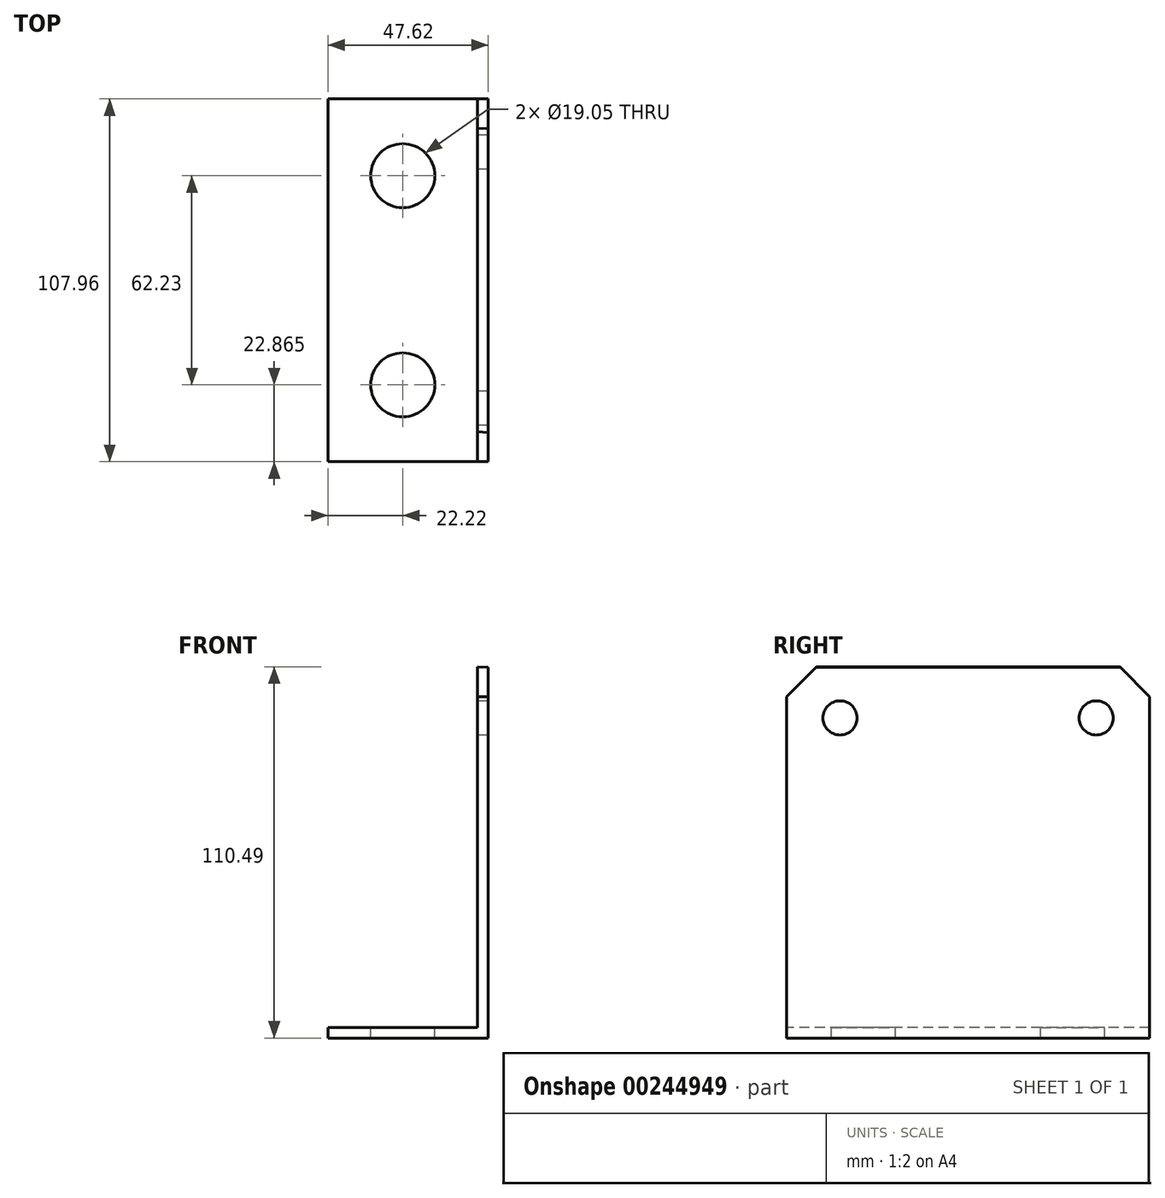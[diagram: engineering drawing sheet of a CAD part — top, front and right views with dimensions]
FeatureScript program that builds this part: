
annotation { "Feature Type Name" : "Feature", "Feature Type Description" : "" }
export const myFeature = defineFeature(function(context is Context, id is Id, definition is map)
    precondition{}
    {
        {
            var Q0;
            Q0=qCreatedBy(makeId("Right.planeOp"),FACE);
            var sketch = newSketch(context, id + "F0", { "sketchPlane" : qUnion([Q0])});
            skLineSegment(sketch, "E0.bottom", {"start": v(28.57, 63.5) * mm, "end": v(-28.57, 63.5) * mm});
            skLineSegment(sketch, "E0.top", {"start": v(53.97, -63.5) * mm, "end": v(-53.97, -63.5) * mm});
            skLineSegment(sketch, "E0.left", {"start": v(53.98, 38.1) * mm, "end": v(53.98, -63.5) * mm});
            skLineSegment(sketch, "E0.right", {"start": v(-53.98, 38.1) * mm, "end": v(-53.97, -63.5) * mm});
            skPoint(sketch, "E0.middle", {"position": v(0, 0) * mm});
            skLineSegment(sketch, "E1", {"start": v(0, 0) * mm, "end": v(0, 94.6) * mm, "construction": true});
            skPoint(sketch, "E1.endSnap0", {"position": v(0, 63.5) * mm});
            skLineSegment(sketch, "E2", {"start": v(-53.98, 38.1) * mm, "end": v(-28.57, 63.5) * mm});
            skLineSegment(sketch, "E3.MirrorCS", {"start": v(53.97, 38.1) * mm, "end": v(28.57, 63.5) * mm});
            skPoint(sketch, "E4.orphan", {"position": v(-53.98, 63.5) * mm});
            skPoint(sketch, "E5.orphan", {"position": v(53.98, 63.5) * mm});
            skSolve(sketch);
        }
        {
            var Q0;
            Q0=qSketchRegion(id+"F0",true);
            extrude(context, id + "F1", {"entities" : qUnion([Q0]), "depth" : 3.17 * mm});
        }
        {
            var Q0;
            Q0=makeQuery(id+"F1.opExtrude","SWEPT_FACE",FACE,{"disambiguationData":[OSD([sQuery(id+"F0.wireOp",EDGE,"E0.right")])]});
            var sketch = newSketch(context, id + "F2", { "sketchPlane" : qUnion([Q0])});
            skLineSegment(sketch, "E6", {"start": v(3.18, -63.5) * mm, "end": v(47.62, -63.5) * mm});
            skLineSegment(sketch, "E7", {"start": v(47.62, -63.5) * mm, "end": v(47.62, -60.33) * mm});
            skLineSegment(sketch, "E8", {"start": v(47.62, -60.33) * mm, "end": v(3.17, -60.33) * mm});
            skLineSegment(sketch, "E9", {"start": v(3.17, -60.33) * mm, "end": v(3.18, -63.5) * mm});
            skSolve(sketch);
        }
        {
            var Q0;
            Q0=qSketchRegion(id+"F2",true);
            var Q1;
            Q1=makeQuery(id+"F1.opExtrude","SWEPT_FACE",FACE,{"disambiguationData":[OSD([sQuery(id+"F0.wireOp",EDGE,"E0.left")])]});
            extrude(context, id + "F3", {"entities" : qUnion([Q0]), "operationType" : NewBodyOperationType.ADD, "endBound" : BoundingType.UP_TO_SURFACE, "oppositeDirection" : true, "endBoundEntityFace" : qUnion([Q1]), "depth" : 25.4 * mm});
        }
        {
            var Q0;
            Q0=makeQuery(id+"F1.opExtrude","CAP_FACE",FACE,{"disambiguationData":[OSD([sQuery(id+"F0.wireOp",EDGE,"E0.bottom"),sQuery(id+"F0.wireOp",EDGE,"E0.top"),sQuery(id+"F0.wireOp",EDGE,"E0.left"),sQuery(id+"F0.wireOp",EDGE,"E0.right")])],"isStart":false});
            var sketch = newSketch(context, id + "F4", { "sketchPlane" : qUnion([Q0])});
            skCircle(sketch, "E10", {"center": v(-38.1, 31.75) * mm, "radius": 5.08 * mm});
            skCircle(sketch, "E11", {"center": v(38.1, 31.75) * mm, "radius": 5.08 * mm});
            skSolve(sketch);
        }
        {
            var Q0;
            Q0=qSketchRegion(id+"F4",true);
            var Q1;
            Q1=makeQuery(id+"F1.opExtrude","CAP_FACE",FACE,{"disambiguationData":[OSD([sQuery(id+"F0.wireOp",EDGE,"E0.bottom"),sQuery(id+"F0.wireOp",EDGE,"E0.top"),sQuery(id+"F0.wireOp",EDGE,"E0.left"),sQuery(id+"F0.wireOp",EDGE,"E0.right"),sQuery(id+"F0.wireOp",EDGE,"E2"),sQuery(id+"F0.wireOp",EDGE,"E3.MirrorCS")])],"isStart":true});
            extrude(context, id + "F5", {"entities" : qUnion([Q0]), "operationType" : NewBodyOperationType.REMOVE, "endBound" : BoundingType.UP_TO_SURFACE, "oppositeDirection" : true, "endBoundEntityFace" : qUnion([Q1]), "depth" : 25.4 * mm});
        }
        {
            var Q0;
            Q0=makeQuery(id+"F3.opExtrude","SWEPT_FACE",FACE,{"disambiguationData":[OSD([sQuery(id+"F2.wireOp",EDGE,"E8")])]});
            var sketch = newSketch(context, id + "F6", { "sketchPlane" : qUnion([Q0])});
            skLineSegment(sketch, "E12", {"start": v(0, 0) * mm, "end": v(0, 50.21) * mm, "construction": true});
            skPoint(sketch, "E13.centerSnap0", {"position": v(25.4, -53.97) * mm});
            skLineSegment(sketch, "E14", {"start": v(0, 0) * mm, "end": v(-46.47, 0) * mm, "construction": true});
            skCircle(sketch, "E15", {"center": v(25.4, 31.11) * mm, "radius": 9.53 * mm});
            skPoint(sketch, "E15.centerSnap0", {"position": v(25.4, 53.97) * mm});
            skCircle(sketch, "E16.MirrorC", {"center": v(25.4, -31.11) * mm, "radius": 9.53 * mm});
            skSolve(sketch);
        }
        {
            var Q0;
            Q0=qSketchRegion(id+"F6",true);
            var Q1;
            Q1=makeQuery(id+"F3.boolean.opBoolean","MERGE",FACE,{"derivedFrom":[makeQuery(id+"F1.opExtrude","SWEPT_FACE",FACE,{"disambiguationData":[OSD([sQuery(id+"F0.wireOp",EDGE,"E0.top")])]}),makeQuery(id+"F3.opExtrude","SWEPT_FACE",FACE,{"disambiguationData":[OSD([sQuery(id+"F2.wireOp",EDGE,"E6")])]})]});
            extrude(context, id + "F7", {"entities" : qUnion([Q0]), "operationType" : NewBodyOperationType.REMOVE, "endBound" : BoundingType.UP_TO_SURFACE, "oppositeDirection" : true, "endBoundEntityFace" : qUnion([Q1]), "depth" : 25.4 * mm});
        }
        {
            var Q0;
            Q0=qSketchRegion(id+"F6",true);
            var Q1;
            Q1=makeQuery(id+"F3.boolean.opBoolean","MERGE",FACE,{"derivedFrom":[makeQuery(id+"F1.opExtrude","SWEPT_FACE",FACE,{"disambiguationData":[OSD([sQuery(id+"F0.wireOp",EDGE,"E0.top")])]}),makeQuery(id+"F3.opExtrude","SWEPT_FACE",FACE,{"disambiguationData":[OSD([sQuery(id+"F2.wireOp",EDGE,"E6")])]})]});
            extrude(context, id + "F8", {"entities" : qUnion([Q0]), "operationType" : NewBodyOperationType.REMOVE, "endBound" : BoundingType.UP_TO_SURFACE, "oppositeDirection" : true, "endBoundEntityFace" : qUnion([Q1]), "depth" : 25.4 * mm});
        }
        {
            var Q0;
            Q0=makeQuery(id+"F1.opExtrude","SWEPT_BODY",BODY,{"disambiguationData":[OSD([sQuery(id+"F0.wireOp",EDGE,"E0.bottom"),sQuery(id+"F0.wireOp",EDGE,"E0.top"),sQuery(id+"F0.wireOp",EDGE,"E0.left"),sQuery(id+"F0.wireOp",EDGE,"E0.right"),sQuery(id+"F0.wireOp",EDGE,"E2"),sQuery(id+"F0.wireOp",EDGE,"E3.MirrorCS")])]});
            var Q1;
            Q1=qCreatedBy(makeId("Right.planeOp"),FACE);
            mirror(context, id + "F9", {"entities" : qUnion([Q0]), "mirrorPlane" : qUnion([Q1])});
        }
        {
            var Q0;
            Q0=makeQuery(id+"F1.opExtrude","SWEPT_BODY",BODY,{"disambiguationData":[OSD([sQuery(id+"F0.wireOp",EDGE,"E0.bottom"),sQuery(id+"F0.wireOp",EDGE,"E0.top"),sQuery(id+"F0.wireOp",EDGE,"E0.left"),sQuery(id+"F0.wireOp",EDGE,"E0.right"),sQuery(id+"F0.wireOp",EDGE,"E2"),sQuery(id+"F0.wireOp",EDGE,"E3.MirrorCS")])]});
            deleteBodies(context, id + "F10", {"entities" : qUnion([Q0])});
        }
        {
            var Q0;
            Q0=makeQuery(id+"F9.opPattern","COPY",FACE,{"derivedFrom":makeQuery(id+"F1.opExtrude","CAP_FACE",FACE,{"disambiguationData":[OSD([sQuery(id+"F0.wireOp",EDGE,"E0.bottom"),sQuery(id+"F0.wireOp",EDGE,"E0.top"),sQuery(id+"F0.wireOp",EDGE,"E0.left"),sQuery(id+"F0.wireOp",EDGE,"E0.right"),sQuery(id+"F0.wireOp",EDGE,"E2"),sQuery(id+"F0.wireOp",EDGE,"E3.MirrorCS")])],"isStart":false}),"instanceName":"1"});
            var sketch = newSketch(context, id + "F11", { "sketchPlane" : qUnion([Q0])});
            skLineSegment(sketch, "E17", {"start": v(-28.57, 63.5) * mm, "end": v(28.57, 63.5) * mm});
            skLineSegment(sketch, "E18", {"start": v(28.57, 63.5) * mm, "end": v(45.09, 46.99) * mm});
            skLineSegment(sketch, "E19", {"start": v(45.09, 46.99) * mm, "end": v(-45.09, 46.99) * mm});
            skLineSegment(sketch, "E20", {"start": v(-45.09, 46.99) * mm, "end": v(-28.58, 63.5) * mm});
            skSolve(sketch);
        }
        {
            var Q0;
            Q0 = qSketchRegion(id + "F11", true);
            var Q1;
            Q1=makeQuery(id+"F9.opPattern","COPY",FACE,{"derivedFrom":makeQuery(id+"F1.opExtrude","CAP_FACE",FACE,{"disambiguationData":[OSD([sQuery(id+"F0.wireOp",EDGE,"E0.bottom"),sQuery(id+"F0.wireOp",EDGE,"E0.top"),sQuery(id+"F0.wireOp",EDGE,"E0.left"),sQuery(id+"F0.wireOp",EDGE,"E0.right"),sQuery(id+"F0.wireOp",EDGE,"E2"),sQuery(id+"F0.wireOp",EDGE,"E3.MirrorCS")])],"isStart":true}),"instanceName":"1"});
            extrude(context, id + "F12", {"entities" : qUnion([Q0]), "operationType" : NewBodyOperationType.REMOVE, "endBound" : BoundingType.UP_TO_SURFACE, "oppositeDirection" : true, "endBoundEntityFace" : qUnion([Q1]), "depth" : 25.4 * mm, "hasDraft" : true, "draftAngle" : 3 * degree});
        }
    });
